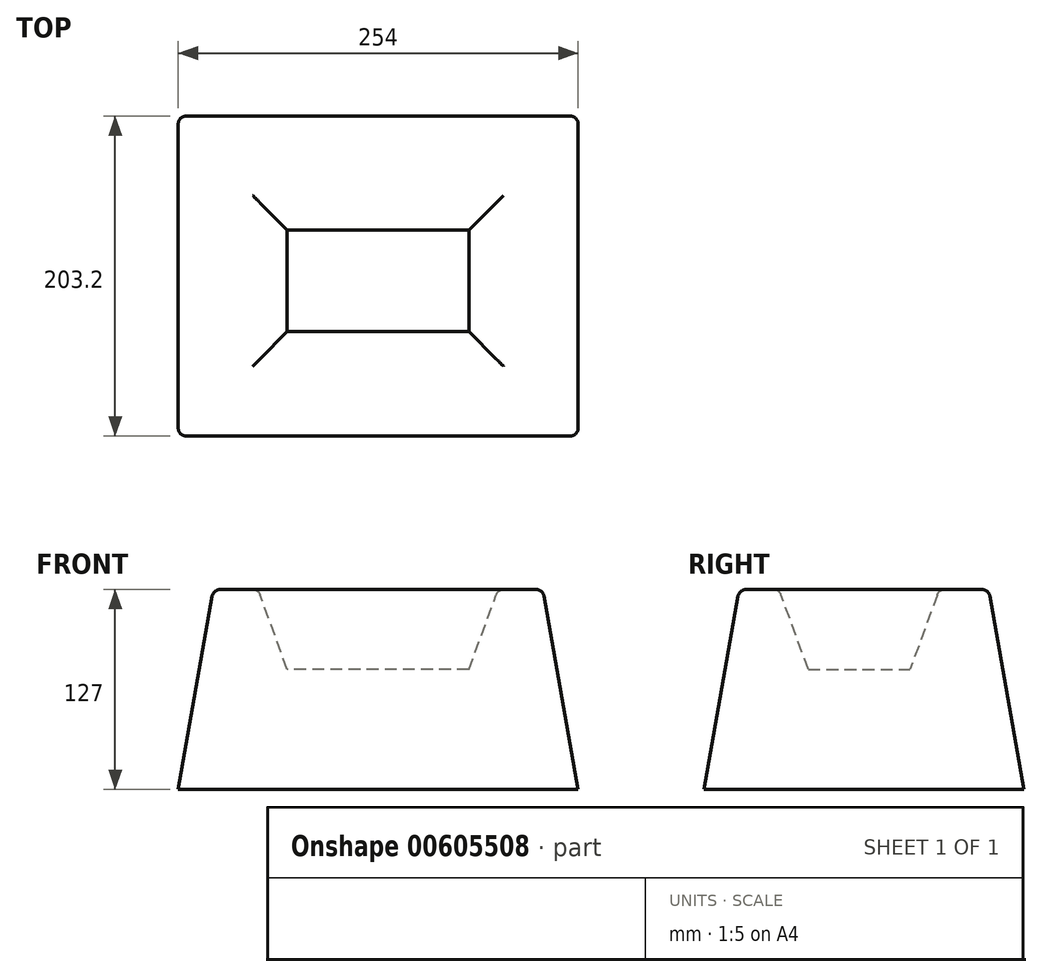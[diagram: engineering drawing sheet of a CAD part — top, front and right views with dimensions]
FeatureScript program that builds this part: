
annotation { "Feature Type Name" : "Feature", "Feature Type Description" : "" }
export const myFeature = defineFeature(function(context is Context, id is Id, definition is map)
    precondition{}
    {
        {
            var Q0;
            Q0=qCreatedBy(makeId("Top.planeOp"),FACE);
            var sketch = newSketch(context, id + "F0", { "sketchPlane" : qUnion([Q0])});
            skLineSegment(sketch, "E0.bottom", {"start": v(127, 101.6) * mm, "end": v(-127, 101.6) * mm});
            skLineSegment(sketch, "E0.top", {"start": v(127, -101.6) * mm, "end": v(-127, -101.6) * mm});
            skLineSegment(sketch, "E0.left", {"start": v(127, 101.6) * mm, "end": v(127, -101.6) * mm});
            skLineSegment(sketch, "E0.right", {"start": v(-127, 101.6) * mm, "end": v(-127, -101.6) * mm});
            skPoint(sketch, "E0.middle", {"position": v(0, 0) * mm});
            skSolve(sketch);
        }
        {
            var Q0;
            Q0=makeQuery(id+"F0.imprint","IMPRINT",FACE,{"disambiguationData":[TD([[makeQuery(id+"F0.imprint","IMPRINT",EDGE,{"derivedFrom":sQuery(id+"F0.wireOp",EDGE,"E0.bottom")}),1.0]])]});
            extrude(context, id + "F1", {"entities" : qUnion([Q0]), "depth" : 127 * mm, "offsetDistance" : 25.4 * mm, "hasDraft" : true, "draftAngle" : 10 * degree, "draftPullDirection" : true});
        }
        {
            var Q0;
            Q0=makeQuery(id+"F1.opExtrude","CAP_FACE",FACE,{"disambiguationData":[OSD([sQuery(id+"F0.wireOp",EDGE,"E0.bottom"),sQuery(id+"F0.wireOp",EDGE,"E0.top"),sQuery(id+"F0.wireOp",EDGE,"E0.left"),sQuery(id+"F0.wireOp",EDGE,"E0.right")])],"isStart":false});
            var sketch = newSketch(context, id + "F2", { "sketchPlane" : qUnion([Q0])});
            skLineSegment(sketch, "E1.bottom", {"start": v(76.2, 47.71) * mm, "end": v(-76.2, 47.71) * mm});
            skLineSegment(sketch, "E1.top", {"start": v(76.2, -53.89) * mm, "end": v(-76.2, -53.89) * mm});
            skLineSegment(sketch, "E1.left", {"start": v(76.2, 47.71) * mm, "end": v(76.2, -53.89) * mm});
            skLineSegment(sketch, "E1.right", {"start": v(-76.2, 47.71) * mm, "end": v(-76.2, -53.89) * mm});
            skPoint(sketch, "E1.middle", {"position": v(0, -3.09) * mm});
            skSolve(sketch);
        }
        {
            var Q0;
            Q0=makeQuery(id+"F2.imprint","IMPRINT",FACE,{"disambiguationData":[TD([[makeQuery(id+"F2.imprint","IMPRINT",EDGE,{"derivedFrom":sQuery(id+"F2.wireOp",EDGE,"E1.bottom")}),1.0]])]});
            extrude(context, id + "F3", {"entities" : qUnion([Q0]), "operationType" : NewBodyOperationType.REMOVE, "oppositeDirection" : true, "depth" : 50.8 * mm, "offsetDistance" : 25.4 * mm, "hasDraft" : true, "draftAngle" : 20 * degree, "draftPullDirection" : true});
        }
        {
            var Q0;
            Q0=makeQuery(id+"F1.opExtrude","CAP_FACE",FACE,{"disambiguationData":[OSD([sQuery(id+"F0.wireOp",EDGE,"E0.bottom"),sQuery(id+"F0.wireOp",EDGE,"E0.top"),sQuery(id+"F0.wireOp",EDGE,"E0.left"),sQuery(id+"F0.wireOp",EDGE,"E0.right")])],"isStart":false});
            var Q1;
            Q1=makeQuery(id+"F1.opExtrude","SWEPT_EDGE",EDGE,{"disambiguationData":[OSD([sQuery(id+"F0.wireOp",EDGE,"E0.bottom"),sQuery(id+"F0.wireOp",EDGE,"E0.right")])]});
            var Q2;
            Q2=makeQuery(id+"F1.opExtrude","SWEPT_EDGE",EDGE,{"disambiguationData":[OSD([sQuery(id+"F0.wireOp",EDGE,"E0.bottom"),sQuery(id+"F0.wireOp",EDGE,"E0.left")])]});
            var Q3;
            Q3=makeQuery(id+"F1.opExtrude","SWEPT_EDGE",EDGE,{"disambiguationData":[OSD([sQuery(id+"F0.wireOp",EDGE,"E0.top"),sQuery(id+"F0.wireOp",EDGE,"E0.left")])]});
            var Q4;
            Q4=makeQuery(id+"F1.opExtrude","SWEPT_EDGE",EDGE,{"disambiguationData":[OSD([sQuery(id+"F0.wireOp",EDGE,"E0.top"),sQuery(id+"F0.wireOp",EDGE,"E0.right")])]});
            fillet(context, id + "F4", {"entities" : qUnion([Q0, Q1, Q2, Q3, Q4]), "radius" : 5.08 * mm, "tangentPropagation" : true, "allowEdgeOverflow" : false});
        }
    });
